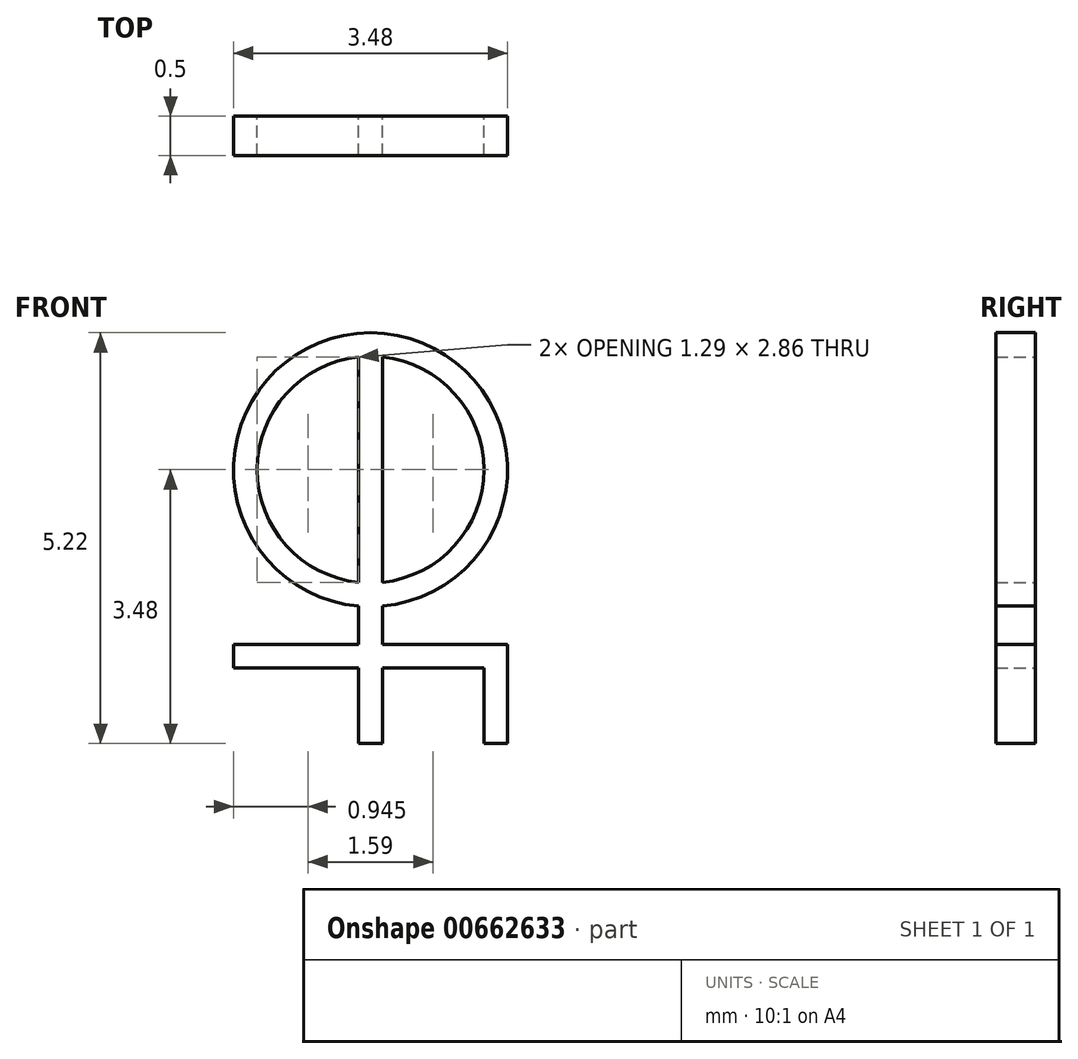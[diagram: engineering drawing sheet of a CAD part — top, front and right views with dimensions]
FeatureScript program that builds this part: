
annotation { "Feature Type Name" : "Feature", "Feature Type Description" : "" }
export const myFeature = defineFeature(function(context is Context, id is Id, definition is map)
    precondition{}
    {
        {
            var Q0;
            Q0=qCreatedBy(makeId("Front.planeOp"),FACE);
            var sketch = newSketch(context, id + "F0", { "sketchPlane" : qUnion([Q0])});
            skArc(sketch, "E0", {"start": v(0.15, -1.43) * mm, "mid": v(1.44, 0) * mm, "end": v(0.15, 1.43) * mm});
            skArc(sketch, "E1.0", {"start": v(0.15, -1.73) * mm, "mid": v(0, 1.74) * mm, "end": v(-0.15, -1.73) * mm});
            skLineSegment(sketch, "E2", {"start": v(-0.15, 1.43) * mm, "end": v(-0.15, -1.43) * mm});
            skLineSegment(sketch, "E3", {"start": v(0.15, 1.43) * mm, "end": v(0.15, -1.43) * mm});
            skLineSegment(sketch, "E4", {"start": v(0.15, -3.48) * mm, "end": v(-0.15, -3.48) * mm});
            skLineSegment(sketch, "E5", {"start": v(-1.74, -2.22) * mm, "end": v(-0.15, -2.22) * mm});
            skLineSegment(sketch, "E6", {"start": v(1.74, -2.22) * mm, "end": v(1.74, -3.48) * mm});
            skLineSegment(sketch, "E7", {"start": v(1.74, -3.48) * mm, "end": v(1.44, -3.48) * mm});
            skLineSegment(sketch, "E8", {"start": v(1.44, -3.48) * mm, "end": v(1.44, -2.52) * mm});
            skLineSegment(sketch, "E9", {"start": v(1.44, -2.52) * mm, "end": v(0.15, -2.52) * mm});
            skLineSegment(sketch, "E10", {"start": v(-1.74, -2.22) * mm, "end": v(-1.74, -2.52) * mm});
            skArc(sketch, "E11.trimOffspring", {"start": v(-0.15, 1.43) * mm, "mid": v(-1.44, 0) * mm, "end": v(-0.15, -1.43) * mm});
            skLineSegment(sketch, "E12.trimOffspring", {"start": v(-0.15, -1.73) * mm, "end": v(-0.15, -2.22) * mm});
            skLineSegment(sketch, "E13.trimOffspring", {"start": v(0.15, -1.73) * mm, "end": v(0.15, -2.22) * mm});
            skLineSegment(sketch, "E14.trimOffspring", {"start": v(-0.15, -2.52) * mm, "end": v(-0.15, -3.48) * mm});
            skLineSegment(sketch, "E15.trimOffspring", {"start": v(0.15, -2.22) * mm, "end": v(1.74, -2.22) * mm});
            skLineSegment(sketch, "E16.trimOffspring", {"start": v(0.15, -2.52) * mm, "end": v(0.15, -3.48) * mm});
            skLineSegment(sketch, "E17.trimOffspring", {"start": v(-0.15, -2.52) * mm, "end": v(-1.74, -2.52) * mm});
            skSolve(sketch);
        }
        {
            var Q0;
            Q0=makeQuery(id+"F0.imprint","IMPRINT",FACE,{"disambiguationData":[TD([[makeQuery(id+"F0.imprint","IMPRINT",EDGE,{"derivedFrom":sQuery(id+"F0.wireOp",EDGE,"E0")}),-1.0]])]});
            extrude(context, id + "F1", {"entities" : qUnion([Q0]), "depth" : .5 * mm, "offsetDistance" : 25 * mm});
        }
    });
